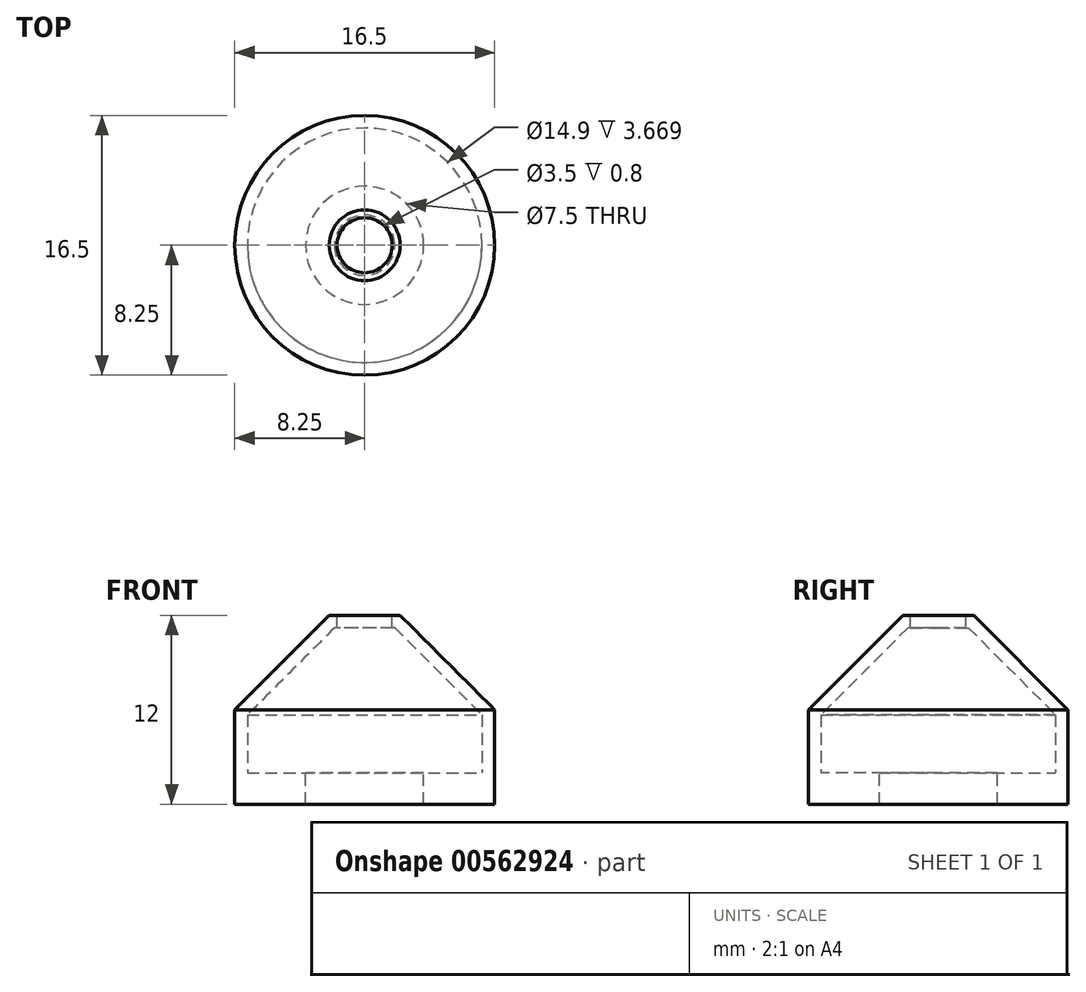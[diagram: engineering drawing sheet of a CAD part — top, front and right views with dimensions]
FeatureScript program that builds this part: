
annotation { "Feature Type Name" : "Feature", "Feature Type Description" : "" }
export const myFeature = defineFeature(function(context is Context, id is Id, definition is map)
    precondition{}
    {
        {
            var Q0;
            Q0=qCreatedBy(makeId("Top.planeOp"),FACE);
            var sketch = newSketch(context, id + "F0", { "sketchPlane" : qUnion([Q0])});
            skCircle(sketch, "E0", {"center": v(0, 0) * mm, "radius": 8.25 * mm});
            skSolve(sketch);
        }
        {
            var Q0;
            Q0 = qSketchRegion(id + "F0", true);
            extrude(context, id + "F1", {"entities" : qUnion([Q0]), "depth" : 10 * mm, "offsetDistance" : 25 * mm});
        }
        {
            var Q0;
            Q0=makeQuery(id+"F1.opExtrude","CAP_EDGE",EDGE,{"disambiguationData":[OSD([sQuery(id+"F0.wireOp",EDGE,"E0")])],"isStart":false});
            chamfer(context, id + "F2", {"entities" : qUnion([Q0]), "width" : 6 * mm, "tangentPropagation" : true});
        }
        {
            var Q0;
            Q0=makeQuery(id+"F1.opExtrude","CAP_FACE",FACE,{"disambiguationData":[OSD([sQuery(id+"F0.wireOp",EDGE,"E0")])],"isStart":true});
            shell(context, id + "F3", {"entities" : qUnion([Q0]), "thickness" : 0.8 * mm});
        }
        {
            var Q0;
            Q0=makeQuery(id+"F1.opExtrude","CAP_FACE",FACE,{"disambiguationData":[OSD([sQuery(id+"F0.wireOp",EDGE,"E0")])],"isStart":false});
            var sketch = newSketch(context, id + "F4", { "sketchPlane" : qUnion([Q0])});
            skCircle(sketch, "E1", {"center": v(0, 0) * mm, "radius": 1.75 * mm});
            skSolve(sketch);
        }
        {
            var Q0;
            Q0 = qSketchRegion(id + "F4", true);
            extrude(context, id + "F5", {"entities" : qUnion([Q0]), "operationType" : NewBodyOperationType.REMOVE, "oppositeDirection" : true, "depth" : 25 * mm, "offsetDistance" : 25 * mm});
        }
        {
            var Q0;
            Q0=qCreatedBy(makeId("Top.planeOp"),FACE);
            var sketch = newSketch(context, id + "F6", { "sketchPlane" : qUnion([Q0])});
            skCircle(sketch, "E2", {"center": v(0, 0) * mm, "radius": 8.25 * mm});
            skCircle(sketch, "E3", {"center": v(0, 0) * mm, "radius": 3.75 * mm});
            skSolve(sketch);
        }
        {
            var Q0;
            Q0 = qSketchRegion(id + "F6", true);
            extrude(context, id + "F7", {"entities" : qUnion([Q0]), "operationType" : NewBodyOperationType.ADD, "oppositeDirection" : true, "depth" : 2 * mm, "offsetDistance" : 25 * mm});
        }
    });
